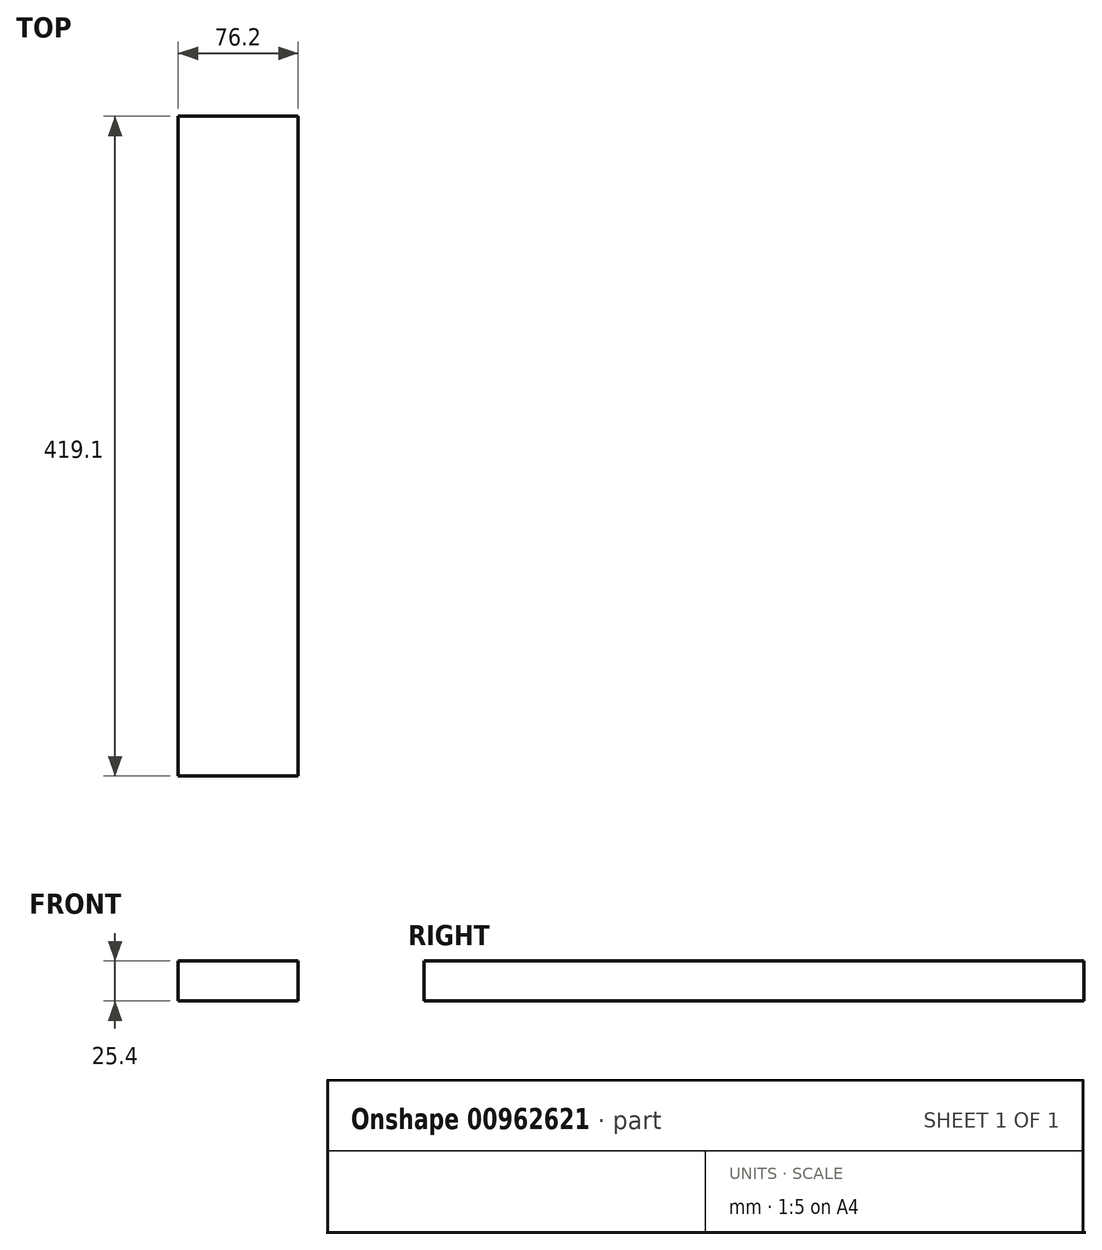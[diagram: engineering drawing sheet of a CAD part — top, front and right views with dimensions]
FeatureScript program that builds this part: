
annotation { "Feature Type Name" : "Feature", "Feature Type Description" : "" }
export const myFeature = defineFeature(function(context is Context, id is Id, definition is map)
    precondition{}
    {
        {
            var Q0;
            Q0=qCreatedBy(makeId("Front.planeOp"),FACE);
            var sketch = newSketch(context, id + "F0", { "sketchPlane" : qUnion([Q0])});
            skLineSegment(sketch, "E0.bottom", {"start": v(38.1, -12.7) * mm, "end": v(-38.1, -12.7) * mm});
            skLineSegment(sketch, "E0.top", {"start": v(38.1, 12.7) * mm, "end": v(-38.1, 12.7) * mm});
            skLineSegment(sketch, "E0.left", {"start": v(38.1, -12.7) * mm, "end": v(38.1, 12.7) * mm});
            skLineSegment(sketch, "E0.right", {"start": v(-38.1, -12.7) * mm, "end": v(-38.1, 12.7) * mm});
            skPoint(sketch, "E0.middle", {"position": v(0, 0) * mm});
            skSolve(sketch);
        }
        {
            var Q0;
            Q0=makeQuery(id+"F0.imprint","IMPRINT",FACE,{"disambiguationData":[TD([[makeQuery(id+"F0.imprint","IMPRINT",EDGE,{"derivedFrom":sQuery(id+"F0.wireOp",EDGE,"E0.bottom")}),-1.0]])]});
            extrude(context, id + "F1", {"entities" : qUnion([Q0]), "depth" : 419.1 * mm, "offsetDistance" : 25.4 * mm});
        }
    });
